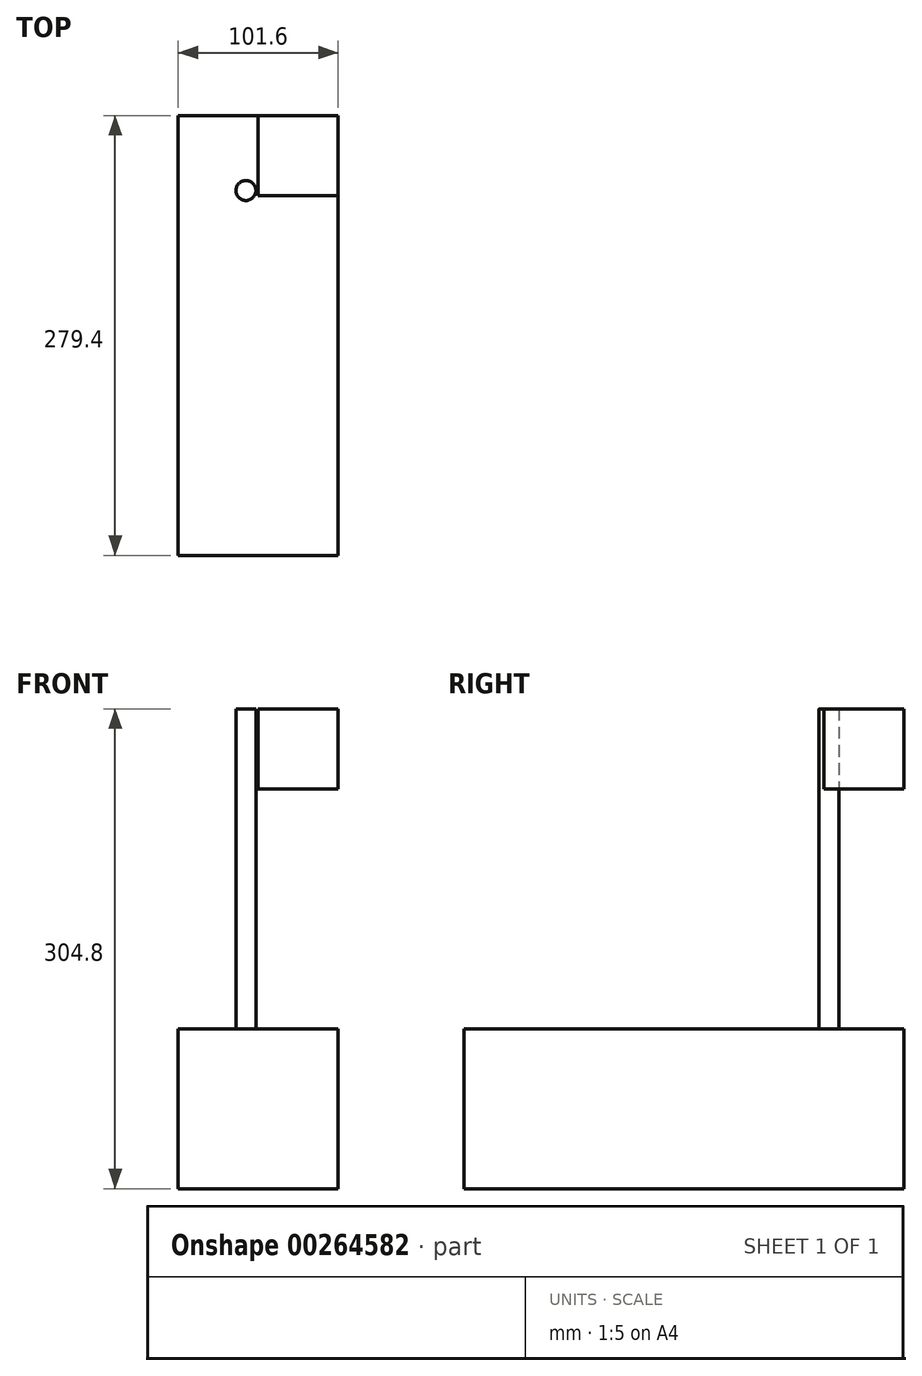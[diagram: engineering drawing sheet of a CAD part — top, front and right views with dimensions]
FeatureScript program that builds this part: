
annotation { "Feature Type Name" : "Feature", "Feature Type Description" : "" }
export const myFeature = defineFeature(function(context is Context, id is Id, definition is map)
    precondition{}
    {
        {
            var Q0;
            Q0=qCreatedBy(makeId("Front.planeOp"),FACE);
            var sketch = newSketch(context, id + "F0", { "sketchPlane" : qUnion([Q0])});
            skLineSegment(sketch, "E0.bottom", {"start": v(0, 0) * mm, "end": v(-101.6, 0) * mm});
            skLineSegment(sketch, "E0.top", {"start": v(0, 101.6) * mm, "end": v(-101.6, 101.6) * mm});
            skLineSegment(sketch, "E0.left", {"start": v(0, 0) * mm, "end": v(0, 101.6) * mm});
            skLineSegment(sketch, "E0.right", {"start": v(-101.6, 0) * mm, "end": v(-101.6, 101.6) * mm});
            skSolve(sketch);
        }
        {
            var Q0;
            Q0=makeQuery(id+"F0.imprint","IMPRINT",FACE,{"disambiguationData":[TD([[makeQuery(id+"F0.imprint","IMPRINT",EDGE,{"derivedFrom":sQuery(id+"F0.wireOp",EDGE,"E0.bottom")}),-1.0]])]});
            extrude(context, id + "F1", {"entities" : qUnion([Q0]), "depth" : 279.4 * mm});
        }
        {
            var Q0;
            Q0=makeQuery(id+"F1.opExtrude","SWEPT_FACE",FACE,{"disambiguationData":[OSD([sQuery(id+"F0.wireOp",EDGE,"E0.top")])]});
            var sketch = newSketch(context, id + "F2", { "sketchPlane" : qUnion([Q0])});
            skCircle(sketch, "E1", {"center": v(-58.6, -47.68) * mm, "radius": 6.35 * mm});
            skSolve(sketch);
        }
        {
            var Q0;
            Q0 = qSketchRegion(id + "F2", true);
            extrude(context, id + "F3", {"entities" : qUnion([Q0]), "operationType" : NewBodyOperationType.ADD, "depth" : 203.2 * mm});
        }
        {
            var Q0;
            Q0=makeQuery(id+"F3.opExtrude","CAP_FACE",FACE,{"disambiguationData":[OSD([sQuery(id+"F2.wireOp",EDGE,"E1")])],"isStart":false});
            var sketch = newSketch(context, id + "F4", { "sketchPlane" : qUnion([Q0])});
            skLineSegment(sketch, "E2.bottom", {"start": v(0, 0) * mm, "end": v(-50.8, 0) * mm});
            skLineSegment(sketch, "E2.top", {"start": v(0, -50.8) * mm, "end": v(-50.8, -50.8) * mm});
            skLineSegment(sketch, "E2.left", {"start": v(0, 0) * mm, "end": v(0, -50.8) * mm});
            skLineSegment(sketch, "E2.right", {"start": v(-50.8, 0) * mm, "end": v(-50.8, -50.8) * mm});
            skSolve(sketch);
        }
        {
            var Q0;
            Q0=makeQuery(id+"F4.imprint","IMPRINT",FACE,{"disambiguationData":[TD([[makeQuery(id+"F4.imprint","IMPRINT",EDGE,{"derivedFrom":sQuery(id+"F4.wireOp",EDGE,"E2.bottom")}),1.0]])]});
            extrude(context, id + "F5", {"entities" : qUnion([Q0]), "oppositeDirection" : true, "depth" : 50.8 * mm});
        }
    });
